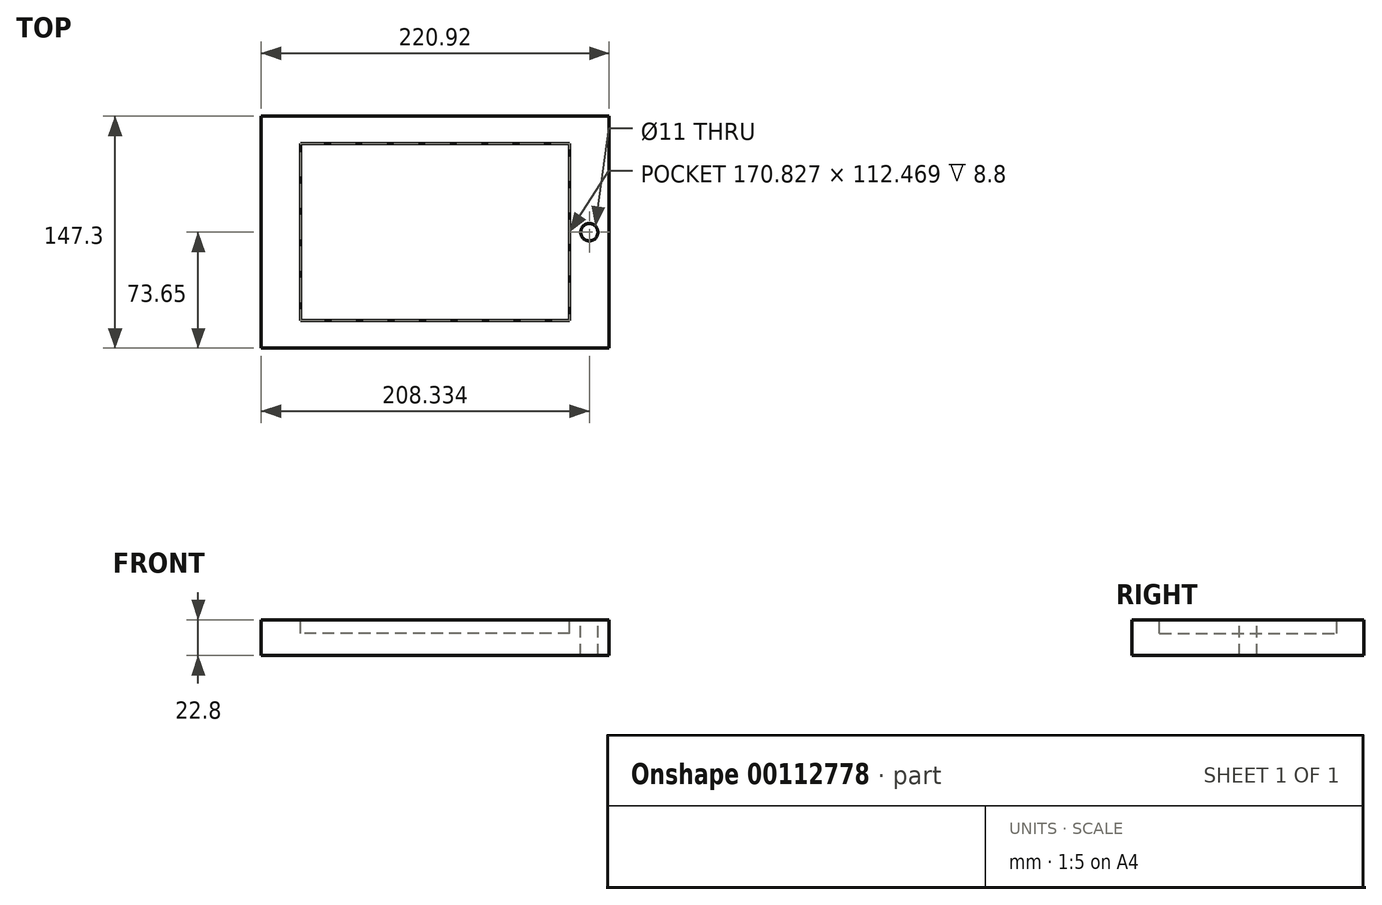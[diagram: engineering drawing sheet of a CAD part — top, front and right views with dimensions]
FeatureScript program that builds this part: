
annotation { "Feature Type Name" : "Feature", "Feature Type Description" : "" }
export const myFeature = defineFeature(function(context is Context, id is Id, definition is map)
    precondition{}
    {
        {
            var Q0;
            Q0=qCreatedBy(makeId("Top.planeOp"),FACE);
            var sketch = newSketch(context, id + "F0", { "sketchPlane" : qUnion([Q0])});
            skLineSegment(sketch, "E0.bottom", {"start": v(110.46, -73.65) * mm, "end": v(-110.46, -73.65) * mm});
            skLineSegment(sketch, "E0.top", {"start": v(110.46, 73.65) * mm, "end": v(-110.46, 73.65) * mm});
            skLineSegment(sketch, "E0.left", {"start": v(110.46, -73.65) * mm, "end": v(110.46, 73.65) * mm});
            skLineSegment(sketch, "E0.right", {"start": v(-110.46, -73.65) * mm, "end": v(-110.46, 73.65) * mm});
            skPoint(sketch, "E0.middle", {"position": v(0, 0) * mm});
            skSolve(sketch);
        }
        {
            var Q0;
            Q0 = qSketchRegion(id + "F0", true);
            extrude(context, id + "F1", {"entities" : qUnion([Q0]), "depth" : 22.8 * mm});
        }
        {
            var Q0;
            Q0=makeQuery(id+"F1.opExtrude","CAP_FACE",FACE,{"disambiguationData":[OSD([sQuery(id+"F0.wireOp",EDGE,"E0.bottom"),sQuery(id+"F0.wireOp",EDGE,"E0.top"),sQuery(id+"F0.wireOp",EDGE,"E0.left"),sQuery(id+"F0.wireOp",EDGE,"E0.right")])],"isStart":false});
            var sketch = newSketch(context, id + "F2", { "sketchPlane" : qUnion([Q0])});
            skLineSegment(sketch, "E1.bottom", {"start": v(85.41, -56.23) * mm, "end": v(-85.41, -56.23) * mm});
            skLineSegment(sketch, "E1.top", {"start": v(85.41, 56.23) * mm, "end": v(-85.41, 56.23) * mm});
            skLineSegment(sketch, "E1.left", {"start": v(85.41, -56.23) * mm, "end": v(85.41, 56.23) * mm});
            skLineSegment(sketch, "E1.right", {"start": v(-85.41, -56.23) * mm, "end": v(-85.41, 56.23) * mm});
            skPoint(sketch, "E1.middle", {"position": v(0, 0) * mm});
            skSolve(sketch);
        }
        {
            var Q0;
            Q0=makeQuery(id+"F2.imprint","IMPRINT",FACE,{"disambiguationData":[TD([[makeQuery(id+"F2.imprint","IMPRINT",EDGE,{"derivedFrom":sQuery(id+"F2.wireOp",EDGE,"E1.bottom")}),-1.0]])]});
            extrude(context, id + "F3", {"entities" : qUnion([Q0]), "operationType" : NewBodyOperationType.REMOVE, "oppositeDirection" : true, "depth" : 8.8 * mm});
        }
        {
            var Q0;
            Q0=makeQuery(id+"F1.opExtrude","CAP_FACE",FACE,{"disambiguationData":[OSD([sQuery(id+"F0.wireOp",EDGE,"E0.bottom"),sQuery(id+"F0.wireOp",EDGE,"E0.top"),sQuery(id+"F0.wireOp",EDGE,"E0.left"),sQuery(id+"F0.wireOp",EDGE,"E0.right")])],"isStart":false});
            var sketch = newSketch(context, id + "F4", { "sketchPlane" : qUnion([Q0])});
            skCircle(sketch, "E2", {"center": v(97.87, 0) * mm, "radius": 8 * mm});
            skSolve(sketch);
        }
        {
            var Q0;
            Q0=sQuery(id+"F4.wireOp",VERTEX,"E2.center");
            var Q1;
            Q1=makeQuery(id+"F1.opExtrude","SWEPT_BODY",BODY,{"disambiguationData":[OSD([sQuery(id+"F0.wireOp",EDGE,"E0.bottom"),sQuery(id+"F0.wireOp",EDGE,"E0.top"),sQuery(id+"F0.wireOp",EDGE,"E0.left"),sQuery(id+"F0.wireOp",EDGE,"E0.right")])]});
            hole(context, id + "F5", {"style" : HoleStyle.SIMPLE, "endStyle" : HoleEndStyle.THROUGH, "standardTappedOrClearance" : lookupTablePath({ "standard" : "ISO", "fit" : "Normal", "size" : "M10", "type" : "Clearance" }), "standardBlindInLast" : lookupTablePath({ "fit" : "Standard", "standard" : "ISO", "size" : "M10", "type" : "Clearance" }), "holeDiameter" : 11 * mm, "locations" : qUnion([Q0]), "scope" : qUnion([Q1]), "isTappedThrough" : true});
        }
    });
